# Revit family: Indoor_Wall Lamp_Santa&Cole_Sylvestrina
name_source: partatom
category: Luminarias
revit_build: Autodesk Revit 2018 (Build: 20170223_1515(x64)
units: mm (PartAtom-declared; Revit-internal decimal feet)

## family parameters
Compartido = No
Corte con vacíos al cargar = No
Cota de conector redondo = Diámetro de uso
Número OmniClass = 23.80.70.00
Origen de luz = Sí
Punto de cálculo de habitación = No
Se basa en plano de trabajo = Sí
Siempre vertical = Sí
Tipo de pieza = Normal
Título OmniClass = Lighting

## types (2) — shared parameters
Archivo de red fotométrica = SYL01 (CL004A21F005G).IES
Cambio de temperatura de color de luz atenuada = <Ninguno>
Carga aparente = 6 VA
Elevación por defecto = 1219 mm
Fabricante = Santa & Cole
Filtro de color = 16777215
Manufacturer website = https://www.santacole.com
Voltaje (90-305 V) = 220 V
Ángulo de inclinación = -90.00°

## per-type parameters (varying)
| type | Assembly instructions - CE | Assembly instructions - UL | Code | Modelo | Technical Information | URL |
| Sylvestrina | https://www.santacole.com | https://www.santacole.com | SYLWA01 | Sylvestrina | https://www.santacole.com | https://www.santacole.com |
| TMM Metálico |  |  |  |  |  |  |

## geometry (parser evidence)
native form markers: Sweep x1
no freeform markers — native parametric forms only
